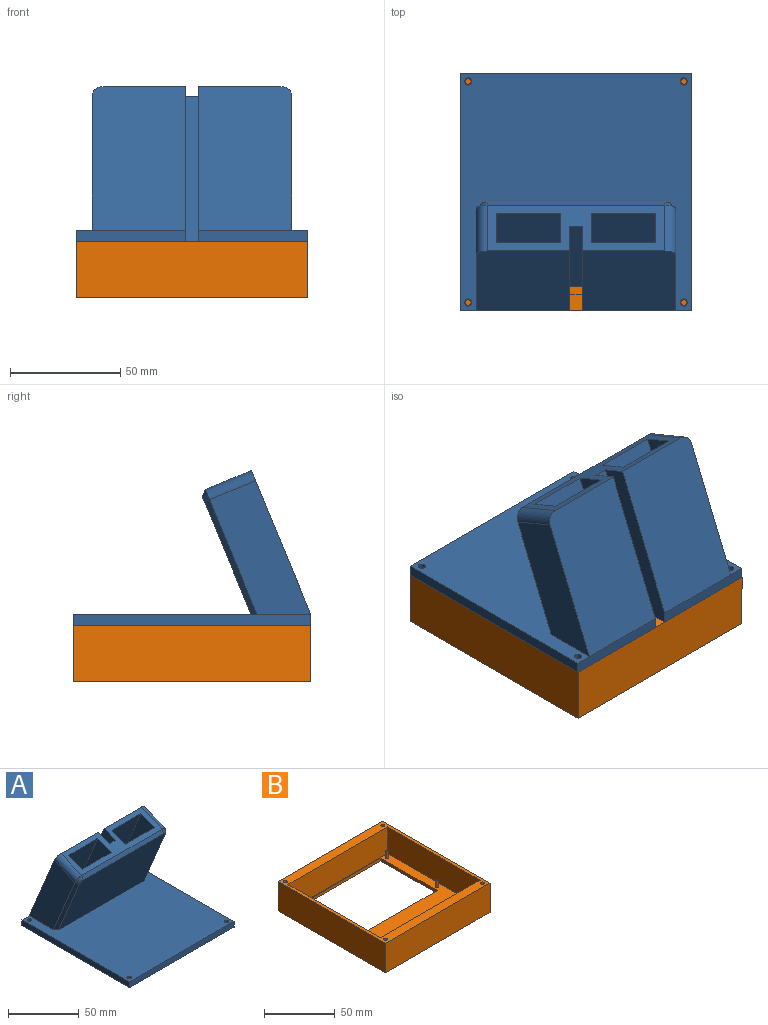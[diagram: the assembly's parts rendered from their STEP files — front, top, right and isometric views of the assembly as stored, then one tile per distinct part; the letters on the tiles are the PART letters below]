
ASSEMBLY  parts=2 mates=1
PART A: 37 faces, bbox 105x107.5x70 mm
  f0: plane 65x42.24mm, normal (0,0.92,0.38), area 2966.4mm2, adj f1,f5,f8,f9,f11
  f1: plane 80.48x20.79mm, normal (0,-0.38,0.92), area 897.8mm2, adj f0,f3,f6,f7,f8,f9,f10,f24
  f2: plane 85.48x53.12mm, normal (0,-0.92,-0.38), area 4912.4mm2, adj f13,f22,f23,f24,f25,f26
  f3: plane 65x42.24mm, normal (0,0.92,0.38), area 2966.4mm2, adj f1,f4,f6,f10,f12
  f4: plane 60.38x45.8mm, normal (-1,0,0), area 1365.6mm2, adj f3,f10,f13,f26
  f5: plane 60.38x45.8mm, normal (1,0,0), area 1365.6mm2, adj f0,f9,f13,f22
  f6: plane 70x38.01mm, normal (1,0,0), area 874.2mm2, adj f1,f3,f7,f12,f15
  f7: plane 65.41x27.09mm, normal (0,0.92,0.38), area 424.8mm2, adj f1,f6,f8,f15
  f8: plane 70x38.01mm, normal (-1,0,0), area 874.2mm2, adj f0,f1,f7,f11,f15
  f9: cylinder r=5mm len=22.7mm, axis (0,-0.92,-0.38), area 176.7mm2, adj f0,f1,f5,f23
  f10: cylinder r=5mm len=22.7mm, axis (0,0.92,0.38), area 176.7mm2, adj f1,f3,f4,f25
  f11: plane 49.48x5mm, normal (0,1,0), area 247.4mm2, adj f0,f8,f13,f15,f17
  f12: plane 49.48x5mm, normal (0,1,0), area 247.4mm2, adj f3,f6,f13,f15,f16
  f13: plane 107.52x104.96mm, normal (0,0,1), area 8810.2mm2, adj f2,f4,f5,f11,f12,f14,f16,f17
  f14: plane 104.96x5mm, normal (0,-1,0), area 524.8mm2, adj f13,f15,f16,f17
  f15: plane 107.52x104.96mm, normal (0,0,-1), area 11186.3mm2, adj f6,f7,f8,f11,f12,f14,f16,f17
  f16: plane 107.52x5mm, normal (-1,0,0), area 537.6mm2, adj f12,f13,f14,f15
  f17: plane 107.52x5mm, normal (1,0,0), area 537.6mm2, adj f11,f13,f14,f15
  f18: cylinder r=1.63mm len=5mm, axis (0,0,-1), area 51.3mm2, adj f13,f15
  f19: cylinder r=1.63mm len=5mm, axis (0,0,-1), area 51.3mm2, adj f13,f15
  f20: cylinder r=1.63mm len=5mm, axis (0,0,-1), area 51.3mm2, adj f13,f15
  f21: cylinder r=1.63mm len=5mm, axis (0,0,-1), area 51.3mm2, adj f13,f15
  f22: plane 51.77x23.75mm, normal (0.71,-0.65,-0.27), area 196.3mm2, adj f2,f5,f13,f23
  f23: cone r=2.5mm half-angle=45deg, axis (0,0.92,0.38), area 20.8mm2, adj f2,f9,f22,f24
  f24: plane 80.48x3.27mm, normal (0,-0.92,0.38), area 284.5mm2, adj f1,f2,f23,f25
  f25: cone r=2.5mm half-angle=45deg, axis (0,0.92,0.38), area 20.8mm2, adj f2,f10,f24,f26
  f26: plane 51.77x23.75mm, normal (-0.71,-0.65,-0.27), area 196.3mm2, adj f2,f4,f13,f25
  f27: plane 53.13x33.1mm, normal (-1,0,0), area 746.7mm2, adj f1,f28,f30,f31
  f28: plane 47.58x29mm, normal (0,-0.92,-0.38), area 1493.5mm2, adj f1,f27,f29,f31
  f29: plane 53.13x33.1mm, normal (1,0,0), area 746.7mm2, adj f1,f28,f30,f31
  f30: plane 47.58x29mm, normal (0,0.92,0.38), area 1493.5mm2, adj f1,f27,f29,f31
  f31: plane 29x13.4mm, normal (0,-0.38,0.92), area 420.5mm2, adj f27,f28,f29,f30
  f32: plane 53.13x33.1mm, normal (-1,0,0), area 746.7mm2, adj f1,f33,f35,f36
  f33: plane 47.58x29mm, normal (0,-0.92,-0.38), area 1493.5mm2, adj f1,f32,f34,f36
  f34: plane 53.13x33.1mm, normal (1,0,0), area 746.7mm2, adj f1,f33,f35,f36
  f35: plane 47.58x29mm, normal (0,0.92,0.38), area 1493.5mm2, adj f1,f32,f34,f36
  f36: plane 29x13.4mm, normal (0,-0.38,0.92), area 420.5mm2, adj f32,f33,f34,f35
PART B: 31 faces, bbox 105x107.5x25.5 mm
  f0: plane 107.52x104.96mm, normal (0,0,1), area 2014.1mm2, adj f1,f2,f7,f8,f9,f10,f21,f22
  f1: plane 92.52x23mm, normal (-1,0,0), area 2128mm2, adj f0,f3,f21,f22
  f2: plane 92.52x23mm, normal (1,0,0), area 2128mm2, adj f0,f3,f21,f22
  f3: plane 99.96x92.52mm, normal (0,0,1), area 4433.8mm2, adj f1,f2,f4,f11,f12,f13,f14,f15
  f4: cylinder r=1mm len=6mm, axis (0,0,1), area 37.7mm2, adj f3,f5
  f5: plane 2x2mm, normal (0,0,1), area 3.1mm2, adj f4
  f6: plane 107.52x104.96mm, normal (0,0,-1), area 6483.4mm2, adj f7,f8,f9,f10,f11,f12,f13,f14
  f7: plane 104.96x25.5mm, normal (0,-1,0), area 2676.5mm2, adj f0,f6,f8,f10
  f8: plane 107.52x25.5mm, normal (1,0,0), area 2741.8mm2, adj f0,f6,f7,f9
  f9: plane 104.96x25.5mm, normal (0,1,0), area 2676.5mm2, adj f0,f6,f8,f10
  f10: plane 107.52x25.5mm, normal (-1,0,0), area 2741.8mm2, adj f0,f6,f7,f9
  f11: plane 56.52x2.5mm, normal (-1,0,0), area 141.3mm2, adj f3,f6,f12,f14
  f12: plane 84.96x2.5mm, normal (0,-1,0), area 212.4mm2, adj f3,f6,f11,f13
  f13: plane 56.52x2.5mm, normal (1,0,0), area 141.3mm2, adj f3,f6,f12,f14
  f14: plane 84.96x2.5mm, normal (0,1,0), area 212.4mm2, adj f3,f6,f11,f13
  f15: cylinder r=1mm len=6mm, axis (0,0,1), area 37.7mm2, adj f3,f16
  f16: plane 2x2mm, normal (0,0,1), area 3.1mm2, adj f15
  f17: cylinder r=1mm len=6mm, axis (0,0,1), area 37.7mm2, adj f3,f18
  f18: plane 2x2mm, normal (0,0,1), area 3.1mm2, adj f17
  f19: cylinder r=1mm len=6mm, axis (0,0,1), area 37.7mm2, adj f3,f20
  f20: plane 2x2mm, normal (0,0,1), area 3.1mm2, adj f19
  f21: plane 99.96x23mm, normal (0,-1,0), area 2299.1mm2, adj f0,f1,f2,f3
  f22: plane 99.96x23mm, normal (0,1,0), area 2299.1mm2, adj f0,f1,f2,f3
  f23: cylinder r=1.35mm len=19.05mm, axis (0,0,1), area 161.6mm2, adj f0,f24
  f24: plane 2.7x2.7mm, normal (0,0,1), area 5.7mm2, adj f23
  f25: cylinder r=1.35mm len=19.05mm, axis (0,0,1), area 161.6mm2, adj f0,f26
  f26: plane 2.7x2.7mm, normal (0,0,1), area 5.7mm2, adj f25
  f27: cylinder r=1.35mm len=19.05mm, axis (0,0,1), area 161.6mm2, adj f0,f28
  f28: plane 2.7x2.7mm, normal (0,0,1), area 5.7mm2, adj f27
  f29: cylinder r=1.35mm len=19.05mm, axis (0,0,1), area 161.6mm2, adj f0,f30
  f30: plane 2.7x2.7mm, normal (0,0,1), area 5.7mm2, adj f29
PLACE A rot(axis=(0,0,-1),180deg) t=(-31.5,-83.08,4.07)mm
PLACE B t=(20.98,2.6,-30.18)mm
MATE slider B.f23 <-> A.f19  axis (0,0,1) through (-27.75,35.11,-8.18)mm
